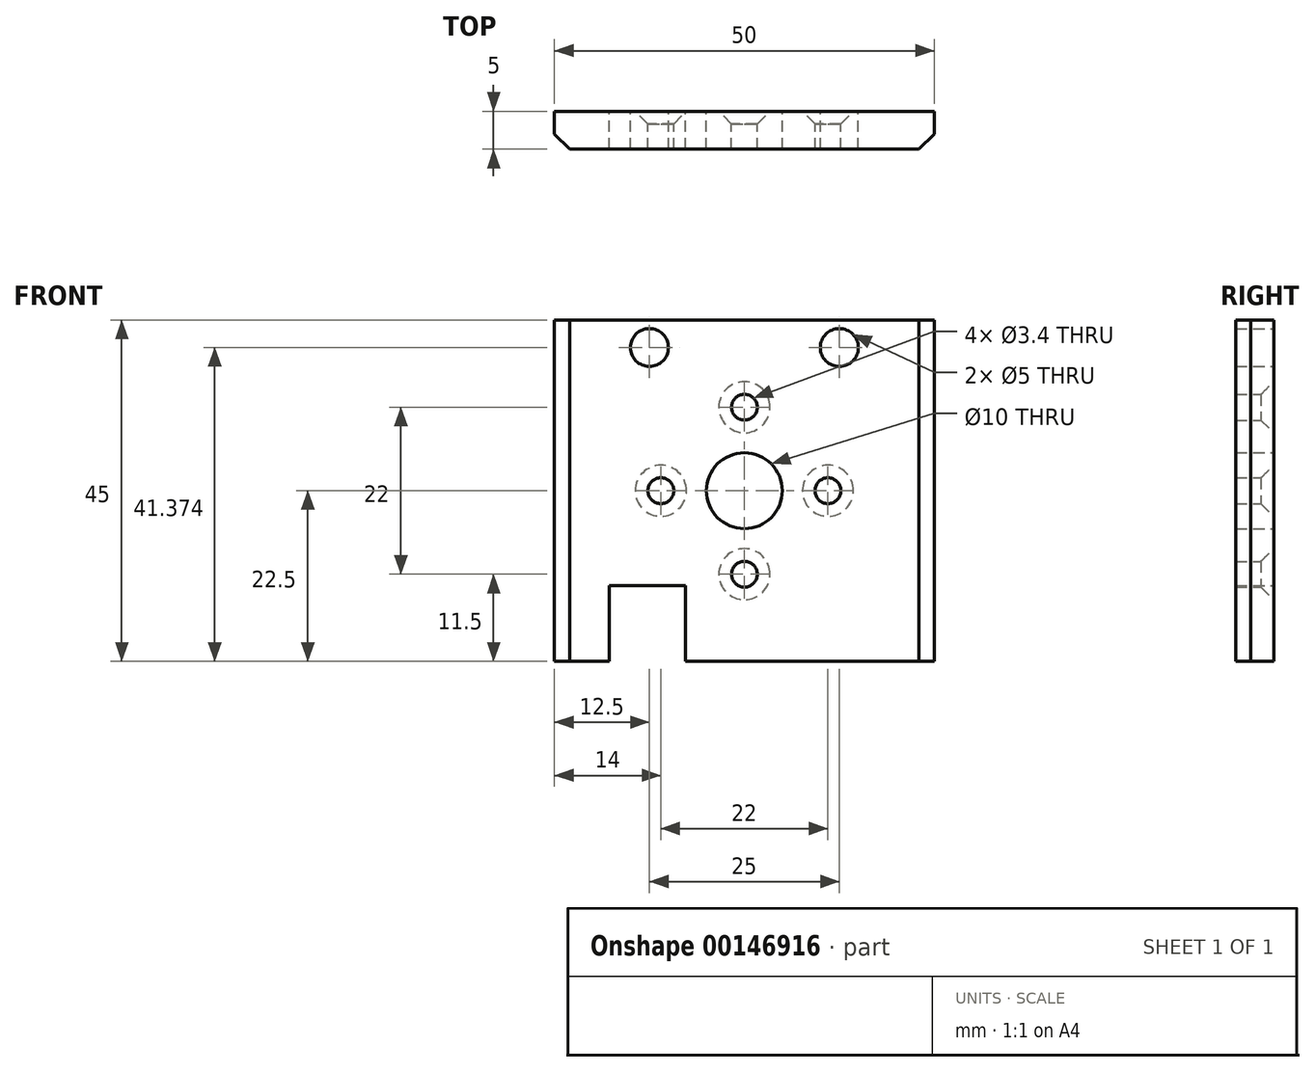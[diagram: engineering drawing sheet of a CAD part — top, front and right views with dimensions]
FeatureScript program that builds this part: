
annotation { "Feature Type Name" : "Feature", "Feature Type Description" : "" }
export const myFeature = defineFeature(function(context is Context, id is Id, definition is map)
    precondition{}
    {
        {
            var Q0;
            Q0=qCreatedBy(makeId("Front.planeOp"),FACE);
            var sketch = newSketch(context, id + "F0", { "sketchPlane" : qUnion([Q0])});
            skLineSegment(sketch, "E0.bottom", {"start": v(25, 22.5) * mm, "end": v(-25, 22.5) * mm});
            skLineSegment(sketch, "E0.top", {"start": v(25, -22.5) * mm, "end": v(-25, -22.5) * mm});
            skLineSegment(sketch, "E0.left", {"start": v(25, 22.5) * mm, "end": v(25, -22.5) * mm});
            skLineSegment(sketch, "E0.right", {"start": v(-25, 22.5) * mm, "end": v(-25, -22.5) * mm});
            skPoint(sketch, "E0.middle", {"position": v(0, 0) * mm});
            skCircle(sketch, "E1", {"center": v(0, 0) * mm, "radius": 5 * mm});
            skCircle(sketch, "E2", {"center": v(-12.5, 18.87) * mm, "radius": 2.5 * mm});
            skCircle(sketch, "E3.MirrorC", {"center": v(12.5, 18.87) * mm, "radius": 2.5 * mm});
            skLineSegment(sketch, "E4", {"start": v(-17.78, -22.5) * mm, "end": v(-17.78, -12.5) * mm});
            skLineSegment(sketch, "E5", {"start": v(-17.78, -12.5) * mm, "end": v(-7.78, -12.5) * mm});
            skLineSegment(sketch, "E6", {"start": v(-7.78, -12.5) * mm, "end": v(-7.78, -22.5) * mm});
            skLineSegment(sketch, "E7", {"start": v(-7.78, -22.5) * mm, "end": v(-17.78, -22.5) * mm});
            skCircle(sketch, "E8", {"center": v(11, 0) * mm, "radius": 1.5 * mm});
            skCircle(sketch, "E9.MirrorC", {"center": v(-11, 0) * mm, "radius": 1.5 * mm});
            skCircle(sketch, "E10", {"center": v(0, 11) * mm, "radius": 1.5 * mm});
            skLineSegment(sketch, "E11", {"start": v(0, 0) * mm, "end": v(0, 23.48) * mm, "construction": true});
            skPoint(sketch, "E11.endSnap0", {"position": v(0, 22.5) * mm});
            skCircle(sketch, "E12.MirrorC", {"center": v(0, -11) * mm, "radius": 1.5 * mm});
            skSolve(sketch);
        }
        {
            var Q0;
            Q0=makeQuery(id+"F0.imprint","IMPRINT",FACE,{"disambiguationData":[TD([[makeQuery(id+"F0.imprint","IMPRINT",EDGE,{"derivedFrom":sQuery(id+"F0.wireOp",EDGE,"E0.bottom")}),1.0]])]});
            extrude(context, id + "F1", {"entities" : qUnion([Q0]), "depth" : 5 * mm});
        }
        {
            var Q0;
            Q0=sQuery(id+"F0.wireOp",VERTEX,"E9.MirrorC.center");
            var Q1;
            Q1=sQuery(id+"F0.wireOp",VERTEX,"E8.center");
            var Q2;
            Q2=sQuery(id+"F0.wireOp",VERTEX,"E10.center");
            var Q3;
            Q3=sQuery(id+"F0.wireOp",VERTEX,"E12.MirrorC.center");
            var Q4;
            Q4=makeQuery(id+"F1.opExtrude","SWEPT_BODY",BODY,{"disambiguationData":[OSD([sQuery(id+"F0.wireOp",EDGE,"E0.bottom"),sQuery(id+"F0.wireOp",EDGE,"E0.top"),sQuery(id+"F0.wireOp",EDGE,"E0.left"),sQuery(id+"F0.wireOp",EDGE,"E0.right"),sQuery(id+"F0.wireOp",EDGE,"E1"),sQuery(id+"F0.wireOp",EDGE,"E2"),sQuery(id+"F0.wireOp",EDGE,"E3.MirrorC"),sQuery(id+"F0.wireOp",EDGE,"E4"),sQuery(id+"F0.wireOp",EDGE,"E5"),sQuery(id+"F0.wireOp",EDGE,"E6"),sQuery(id+"F0.wireOp",EDGE,"E8"),sQuery(id+"F0.wireOp",EDGE,"E9.MirrorC"),sQuery(id+"F0.wireOp",EDGE,"E10"),sQuery(id+"F0.wireOp",EDGE,"E12.MirrorC")])]});
            hole(context, id + "F2", {"style" : HoleStyle.C_SINK, "endStyle" : HoleEndStyle.THROUGH, "oppositeDirection" : true, "standardTappedOrClearance" : lookupTablePath({ "fit" : "Normal", "standard" : "ISO", "size" : "M3", "type" : "Clearance" }), "standardBlindInLast" : lookupTablePath({ "fit" : "Normal", "standard" : "ISO", "engagement" : "75%", "pitch" : "0.5 mm", "size" : "M3", "type" : "Clearance & tapped" }), "holeDiameter" : 3.4 * mm, "cSinkDiameter" : 6.72 * mm, "cSinkAngle" : 90 * degree, "majorDiameter" : 5 * mm, "isTappedThrough" : true, "tappedDepth" : 12 * mm, "tapClearance" : 3, "locations" : qUnion([Q0, Q1, Q2, Q3]), "scope" : qUnion([Q4])});
        }
        {
            var Q0;
            Q0=makeQuery(id+"F1.opExtrude","CAP_EDGE",EDGE,{"disambiguationData":[OSD([sQuery(id+"F0.wireOp",EDGE,"E0.left")])],"isStart":false});
            var Q1;
            Q1=makeQuery(id+"F1.opExtrude","CAP_EDGE",EDGE,{"disambiguationData":[OSD([sQuery(id+"F0.wireOp",EDGE,"E0.right")])],"isStart":false});
            chamfer(context, id + "F3", {"entities" : qUnion([Q0, Q1]), "width" : 2 * mm, "tangentPropagation" : true});
        }
    });
